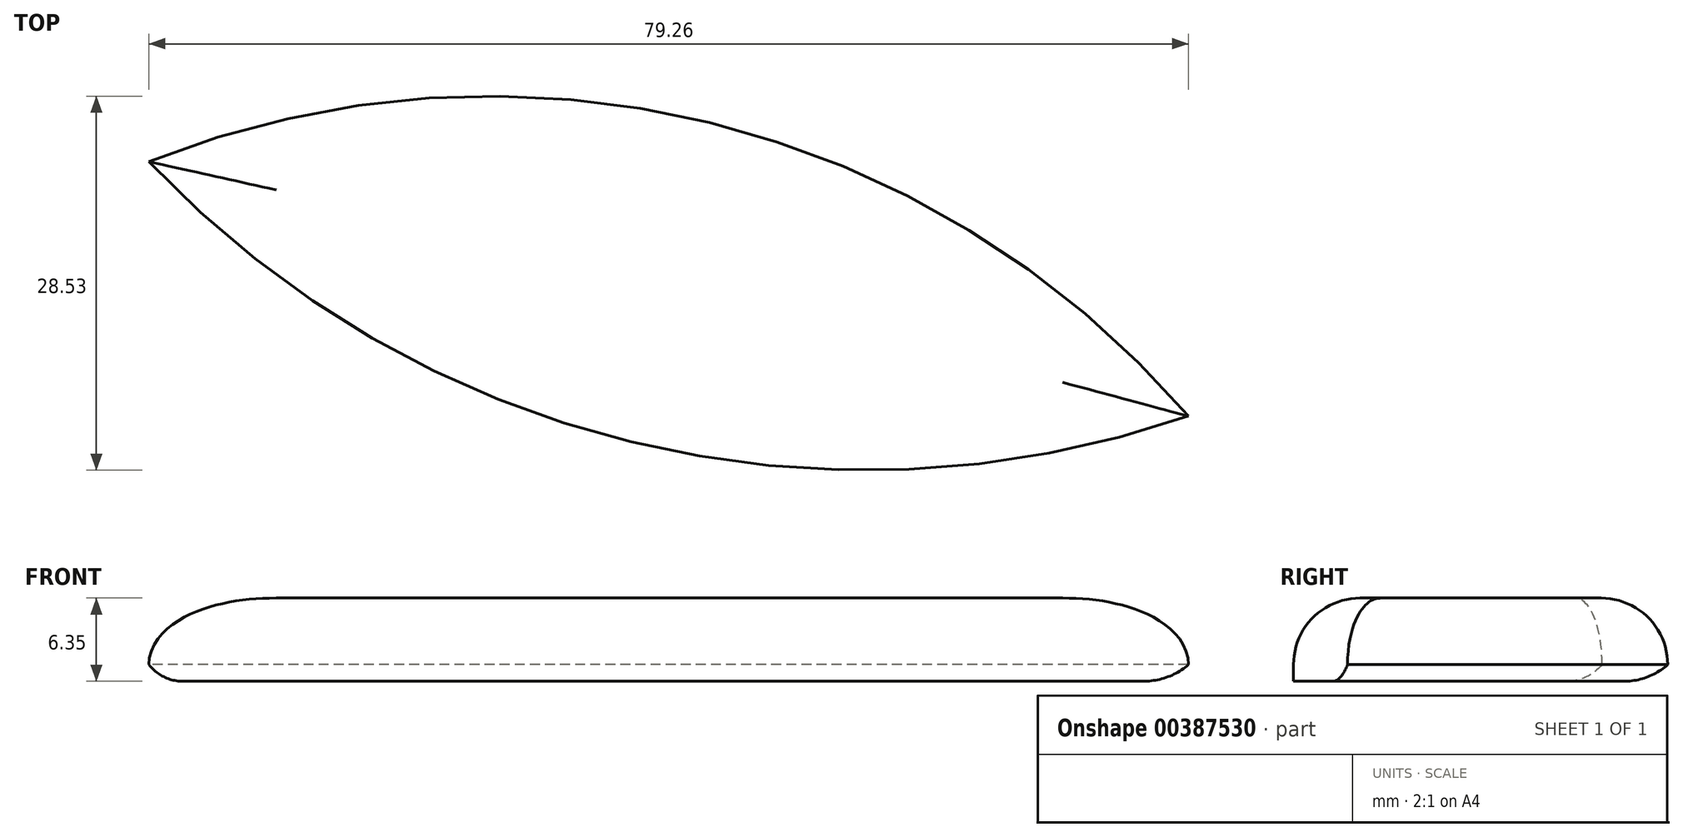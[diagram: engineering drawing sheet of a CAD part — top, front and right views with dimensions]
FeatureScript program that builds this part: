
annotation { "Feature Type Name" : "Feature", "Feature Type Description" : "" }
export const myFeature = defineFeature(function(context is Context, id is Id, definition is map)
    precondition{}
    {
        {
            var Q0;
            Q0=qCreatedBy(makeId("Top.planeOp"),FACE);
            var sketch = newSketch(context, id + "F0", { "sketchPlane" : qUnion([Q0])});
            skArc(sketch, "E0", {"start": v(-137.74, 49.98) * mm, "mid": v(-100.97, 28.61) * mm, "end": v(-58.48, 30.57) * mm});
            skArc(sketch, "E1", {"start": v(-58.48, 30.57) * mm, "mid": v(-95, 52.97) * mm, "end": v(-137.74, 49.98) * mm});
            skSolve(sketch);
        }
        {
            var Q0;
            Q0=makeQuery(id+"F0.imprint","IMPRINT",FACE,{"disambiguationData":[TD([[makeQuery(id+"F0.imprint","IMPRINT",EDGE,{"derivedFrom":sQuery(id+"F0.wireOp",EDGE,"E0")}),1.0]])]});
            extrude(context, id + "F1", {"entities" : qUnion([Q0]), "depth" : 6.35 * mm});
        }
        {
            var Q0;
            Q0=makeQuery(id+"F1.opExtrude","CAP_EDGE",EDGE,{"disambiguationData":[OSD([sQuery(id+"F0.wireOp",EDGE,"E0")])],"isStart":false});
            var Q1;
            Q1=makeQuery(id+"F1.opExtrude","CAP_EDGE",EDGE,{"disambiguationData":[OSD([sQuery(id+"F0.wireOp",EDGE,"E1")])],"isStart":false});
            fillet(context, id + "F2", {"entities" : qUnion([Q0, Q1]), "radius" : 5.08 * mm, "tangentPropagation" : true, "allowEdgeOverflow" : false});
        }
        {
            var Q0;
            {var subQ0=sQuery(id+"F0.wireOp",EDGE,"E0");Q0=makeQuery(id+"F2.opFillet","BLEND_EDGE",EDGE,{"blendedFrom":[makeQuery(id+"F1.opExtrude","CAP_EDGE",EDGE,{"disambiguationData":[OSD([subQ0])],"isStart":false}),makeQuery(id+"F1.opExtrude","SWEPT_FACE",FACE,{"disambiguationData":[OSD([subQ0])]})],"blendedInto":[makeQuery(id+"F1.opExtrude","SWEPT_FACE",FACE,{"disambiguationData":[OSD([subQ0])]})]});}
            var Q1;
            Q1=makeQuery(id+"F1.opExtrude","CAP_EDGE",EDGE,{"disambiguationData":[OSD([sQuery(id+"F0.wireOp",EDGE,"E1")])],"isStart":true});
            fillet(context, id + "F3", {"entities" : qUnion([Q0, Q1]), "radius" : 5.08 * mm, "tangentPropagation" : true, "allowEdgeOverflow" : false});
        }
    });
